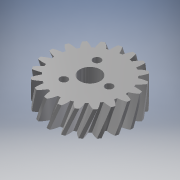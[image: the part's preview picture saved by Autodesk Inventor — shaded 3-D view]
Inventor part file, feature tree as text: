
AUTODESK INVENTOR PART (.ipt)
format: ipt  version: 2017 SP1 (Build 210196100, 196)  size: 836,096 bytes
history: native  units: mm (DEFAULTED — no unit token found)
features: sketch x4, plane x3, other x3, extrude x2, hole x1
ambient origin geometry x8: Origin, YZ Plane, XZ Plane, XY Plane, X Axis, Y Axis, Z Axis, Center Point
bodies: Solid1 (feature_tree)
feature tree (13):
  extrude  "Extrusion1"  Depth=10.0mm TaperAngle=0.0deg
  plane  "Work Plane2"
  plane  "Work Plane8"
  plane  "Work Plane9"
  other  "Engrenage cylindrique"
  extrude  "Extrusion2"  Depth=10.0mm TaperAngle=0.0deg
  hole  "Perçage1"  [1 undecoded]
  sketch  "Sketch1"  dims[d0=32.749068mm d1=10.0mm d2=0.0mm]
  sketch  "Sketch2"  dims[d3=30.066593mm d4=10.0mm d5=0.0mm d16=30.066593mm d17=0.0mm d34=1.570796mm d39=0.0mm d41=0.0mm d43=30.066593mm d46=30.066593mm d47=0.0mm d48=0.0mm d49=8.0mm d50=10.0mm d51=10.0mm d52=0.0mm d53=15.0mm d54=30.0mm d56=360.0deg d58=3.0mm d59=6.0mm d60=4.0mm d61=2.0mm d62=90.0deg d63=10.0mm d64=20.594885mm]
  other  "Srf1"
  sketch  "Esquisse3"
  sketch  "Esquisse4"
  other  "Diamètre primitif"
note: 1 required parameter value undecoded (feature->parameter linkage not recoverable at this tier; creation-order binding heuristic only, values carry confidence <= 0.55)
